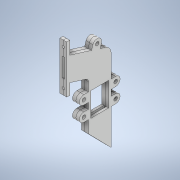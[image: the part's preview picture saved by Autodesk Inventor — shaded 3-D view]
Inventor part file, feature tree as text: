
AUTODESK INVENTOR PART (.ipt)
format: ipt  version: 2020 (Build 240168000, 168)  size: 467,456 bytes
history: native  units: in
note: dims shown in document units (in); Inventor stores cm internally (conversion verified against a paired STEP export)
features: sketch x11, extrude x6, hole x5, split x4, boolean_combine x2, shell x1, fillet x1
ambient origin geometry x8: Origin, YZ Plane, XZ Plane, XY Plane, X Axis, Y Axis, Z Axis, Center Point
bodies: Solid1 (feature_tree), Solid2 (feature_tree), Solid3 (feature_tree), Solid4 (feature_tree), Solid5 (feature_tree), Solid6 (feature_tree), Solid7 (feature_tree)
feature tree (30):
  extrude  "Extrusion1"  Depth=0.3937in
  shell  "Shell2"  Thickness=1.1811in
  extrude  "Extrusion2"  Depth=0.3937in
  split  "Split1"
  fillet  "Fillet1"  Radius=1.5748in
  extrude  "Extrusion3"  Depth=0.1575in
  sketch  "Sketch6"  dims[d11=1.378in d12=0.315in d13=0.0in]
  extrude  "Extrusion5"  Depth=1.378in TaperAngle=0.0deg
  hole  "Hole1"  [1 undecoded]
  hole  "Hole2"  [1 undecoded]
  extrude  "Extrusion7"  Depth=0.0787in
  hole  "Hole3"  [1 undecoded]
  hole  "Hole4"  [1 undecoded]
  hole  "Hole5"  [1 undecoded]
  boolean_combine  "Combine1"
  extrude  "Extrusion9"  Depth=0.5906in
  split  "Split2"
  boolean_combine  "Combine2"
  split  "Split3"
  split  "Split4"
  sketch  "Sketch1"  dims[d0=7.874in d1=0.3937in d2=1.1811in]
  sketch  "Sketch4"  dims[d3=1.1811in d4=0.3937in d5=1.5748in]
  sketch  "Sketch5"  dims[d6=0.1378in d7=0.0in d10=0.1575in]
  sketch  "Sketch7"  dims[d17=0.3937in d18=0.5906in]
  sketch  "Sketch8"  dims[d19=0.4528in d20=0.0in d22=0.5906in]
  sketch  "Sketch14"  dims[d27=0.4528in d28=0.0in]
  sketch  "Sketch15"  dims[d29=0.2362in d30=0.2362in d31=0.1575in d32=0.0787in d33=90.0deg d34=0.315in d35=0.8108in]
  sketch  "Sketch16"  dims[d36=0.2362in d37=0.2362in d38=0.1575in d39=0.0787in d40=90.0deg d41=0.315in d42=0.8108in d46=0.7874in]
  sketch  "Sketch17"  dims[d47=0.4528in d48=0.0in d49=0.1969in]
  sketch  "Sketch19"  dims[d50=0.1575in d51=0.625in d52=0.1575in d53=0.0787in d54=90.0deg d55=0.5906in d56=0.8108in d57=0.5906in d58=0.0in d59=0.2362in d60=0.2362in d61=0.1575in d62=0.0787in d63=90.0deg d64=0.5906in d65=0.8108in d66=0.5906in d67=0.5906in d68=0.5906in d69=0.3937in d70=0.2362in d71=0.2362in d72=0.1575in d73=0.0787in d74=90.0deg d75=0.5906in d76=0.8108in d79=0.0in d80=0.0in d84=4.9803in]
note: 5 required parameter values undecoded (feature->parameter linkage not recoverable at this tier; creation-order binding heuristic only, values carry confidence <= 0.55)
